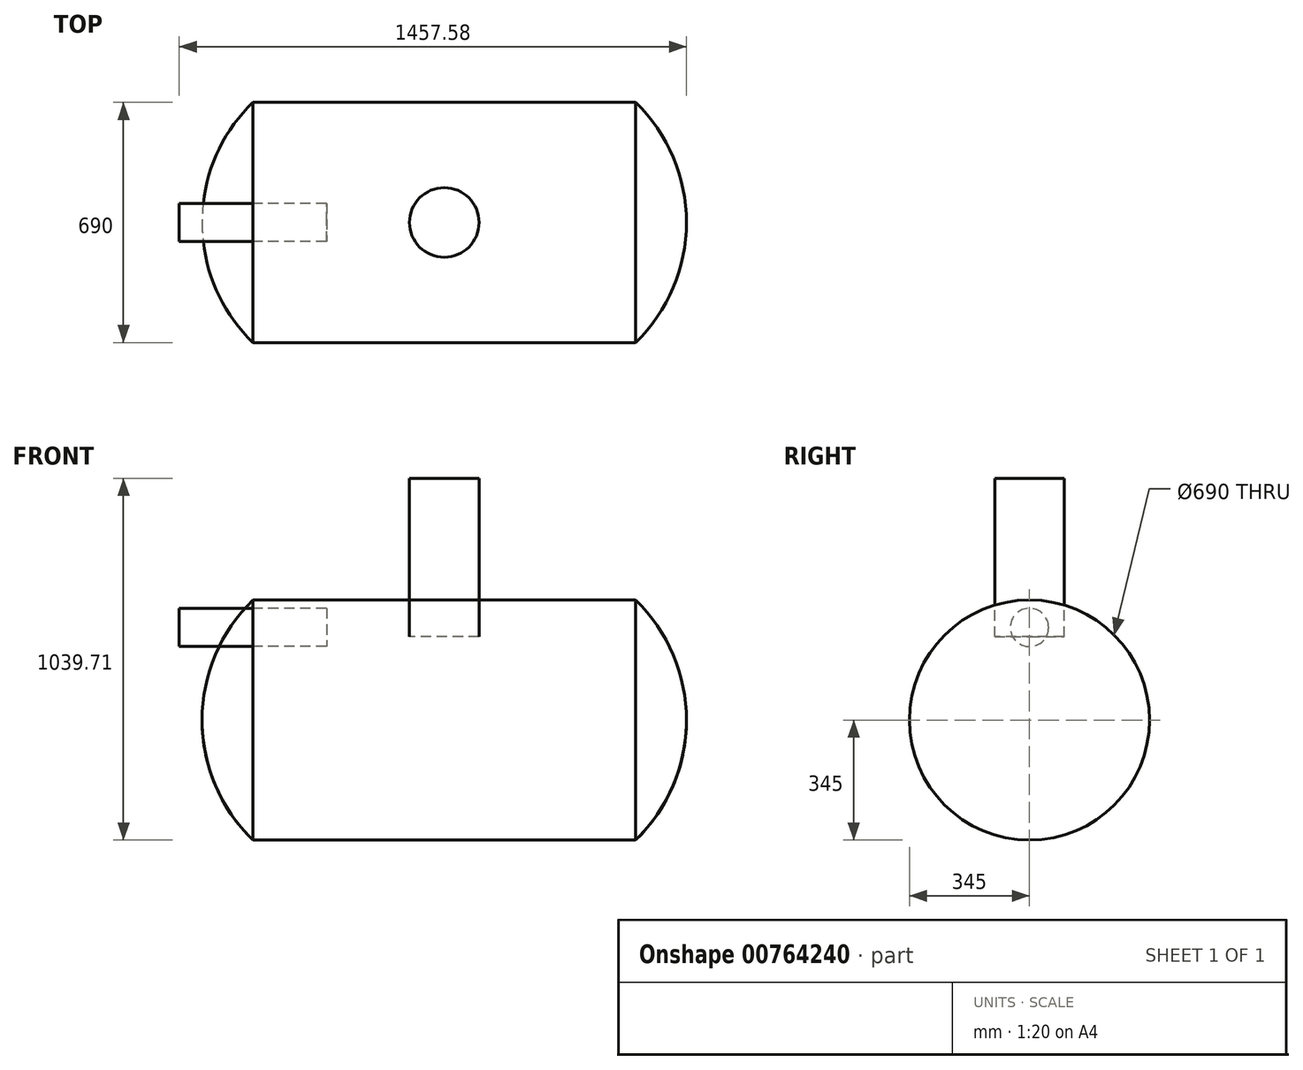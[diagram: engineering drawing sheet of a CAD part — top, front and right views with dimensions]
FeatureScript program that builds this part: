
annotation { "Feature Type Name" : "Feature", "Feature Type Description" : "" }
export const myFeature = defineFeature(function(context is Context, id is Id, definition is map)
    precondition{}
    {
        {
            var Q0;
            Q0=qCreatedBy(makeId("Front.planeOp"),FACE);
            var sketch = newSketch(context, id + "F0", { "sketchPlane" : qUnion([Q0])});
            skLineSegment(sketch, "E0.bottom", {"start": v(-550, 345) * mm, "end": v(550, 345) * mm});
            skLineSegment(sketch, "E0.top", {"start": v(-550, -345) * mm, "end": v(550, -345) * mm});
            skLineSegment(sketch, "E0.left", {"start": v(-550, 345) * mm, "end": v(-550, -345) * mm});
            skLineSegment(sketch, "E0.right", {"start": v(550, 345) * mm, "end": v(550, -345) * mm});
            skLineSegment(sketch, "E1.bottom", {"start": v(-761.58, 321.12) * mm, "end": v(-338.42, 321.12) * mm});
            skLineSegment(sketch, "E1.top", {"start": v(-761.58, 211.12) * mm, "end": v(-338.42, 211.12) * mm});
            skLineSegment(sketch, "E1.left", {"start": v(-761.58, 321.12) * mm, "end": v(-761.58, 211.12) * mm});
            skLineSegment(sketch, "E1.right", {"start": v(-338.42, 321.12) * mm, "end": v(-338.42, 211.12) * mm});
            skPoint(sketch, "E1.middle", {"position": v(-550, 266.12) * mm});
            skLineSegment(sketch, "E2.bottom", {"start": v(-100, 694.7) * mm, "end": v(100, 694.7) * mm});
            skLineSegment(sketch, "E2.top", {"start": v(-100, 239.34) * mm, "end": v(100, 239.34) * mm});
            skLineSegment(sketch, "E2.left", {"start": v(-100, 694.7) * mm, "end": v(-100, 239.34) * mm});
            skLineSegment(sketch, "E2.right", {"start": v(100, 694.7) * mm, "end": v(100, 239.34) * mm});
            skPoint(sketch, "E2.middle", {"position": v(0, 467.02) * mm});
            skLineSegment(sketch, "E3", {"start": v(-550, 0) * mm, "end": v(550, 0) * mm});
            skLineSegment(sketch, "E4", {"start": v(-550, 0) * mm, "end": v(-696, 0) * mm});
            skLineSegment(sketch, "E5", {"start": v(550, 0) * mm, "end": v(696, 0) * mm});
            skLineSegment(sketch, "E6", {"start": v(0, 239.34) * mm, "end": v(0, 694.7) * mm});
            skLineSegment(sketch, "E7", {"start": v(-338.42, 266.12) * mm, "end": v(-761.58, 266.12) * mm});
            skPoint(sketch, "E8", {"position": v(-696, 0) * mm});
            skArc(sketch, "E9", {"start": v(-550, 345) * mm, "mid": v(-658, 187.31) * mm, "end": v(-696, 0) * mm});
            skArc(sketch, "E10", {"start": v(550, -345) * mm, "mid": v(658, -187.31) * mm, "end": v(696, 0) * mm});
            skArc(sketch, "E11", {"start": v(696, 0) * mm, "mid": v(658, 187.31) * mm, "end": v(550, 345) * mm});
            skArc(sketch, "E12", {"start": v(-696, 0) * mm, "mid": v(-658, -187.31) * mm, "end": v(-550, -345) * mm});
            skSolve(sketch);
        }
        {
            var Q0;
            Q0=sQuery(id+"F0.wireOp",EDGE,"E2.right");
            var Q1;
            Q1=sQuery(id+"F0.wireOp",EDGE,"E6");
            revolve(context, id + "F1", {"bodyType" : ToolBodyType.SURFACE, "surfaceOperationType" : NewSurfaceOperationType.NEW, "surfaceEntities" : qUnion([Q0]), "axis" : qUnion([Q1]), "revolveType" : RevolveType.FULL});
        }
        {
            var Q0;
            Q0=sQuery(id+"F0.wireOp",EDGE,"E1.bottom");
            var Q1;
            Q1=sQuery(id+"F0.wireOp",EDGE,"E7");
            revolve(context, id + "F2", {"bodyType" : ToolBodyType.SURFACE, "surfaceOperationType" : NewSurfaceOperationType.NEW, "surfaceEntities" : qUnion([Q0]), "axis" : qUnion([Q1]), "revolveType" : RevolveType.FULL});
        }
        {
            var Q0;
            Q0=sQuery(id+"F0.wireOp",EDGE,"E0.top");
            var Q1;
            Q1=sQuery(id+"F0.wireOp",EDGE,"E3");
            revolve(context, id + "F3", {"bodyType" : ToolBodyType.SURFACE, "surfaceOperationType" : NewSurfaceOperationType.NEW, "surfaceEntities" : qUnion([Q0]), "axis" : qUnion([Q1]), "revolveType" : RevolveType.FULL});
        }
        {
            var Q0;
            Q0=sQuery(id+"F0.wireOp",EDGE,"E12");
            var Q1;
            Q1=sQuery(id+"F0.wireOp",EDGE,"E4");
            revolve(context, id + "F4", {"bodyType" : ToolBodyType.SURFACE, "surfaceOperationType" : NewSurfaceOperationType.NEW, "surfaceEntities" : qUnion([Q0]), "axis" : qUnion([Q1]), "revolveType" : RevolveType.FULL});
        }
        {
            var Q0;
            Q0=sQuery(id+"F0.wireOp",EDGE,"E10");
            var Q1;
            Q1=sQuery(id+"F0.wireOp",EDGE,"E5");
            revolve(context, id + "F5", {"bodyType" : ToolBodyType.SURFACE, "surfaceOperationType" : NewSurfaceOperationType.NEW, "surfaceEntities" : qUnion([Q0]), "axis" : qUnion([Q1]), "revolveType" : RevolveType.FULL});
        }
    });
